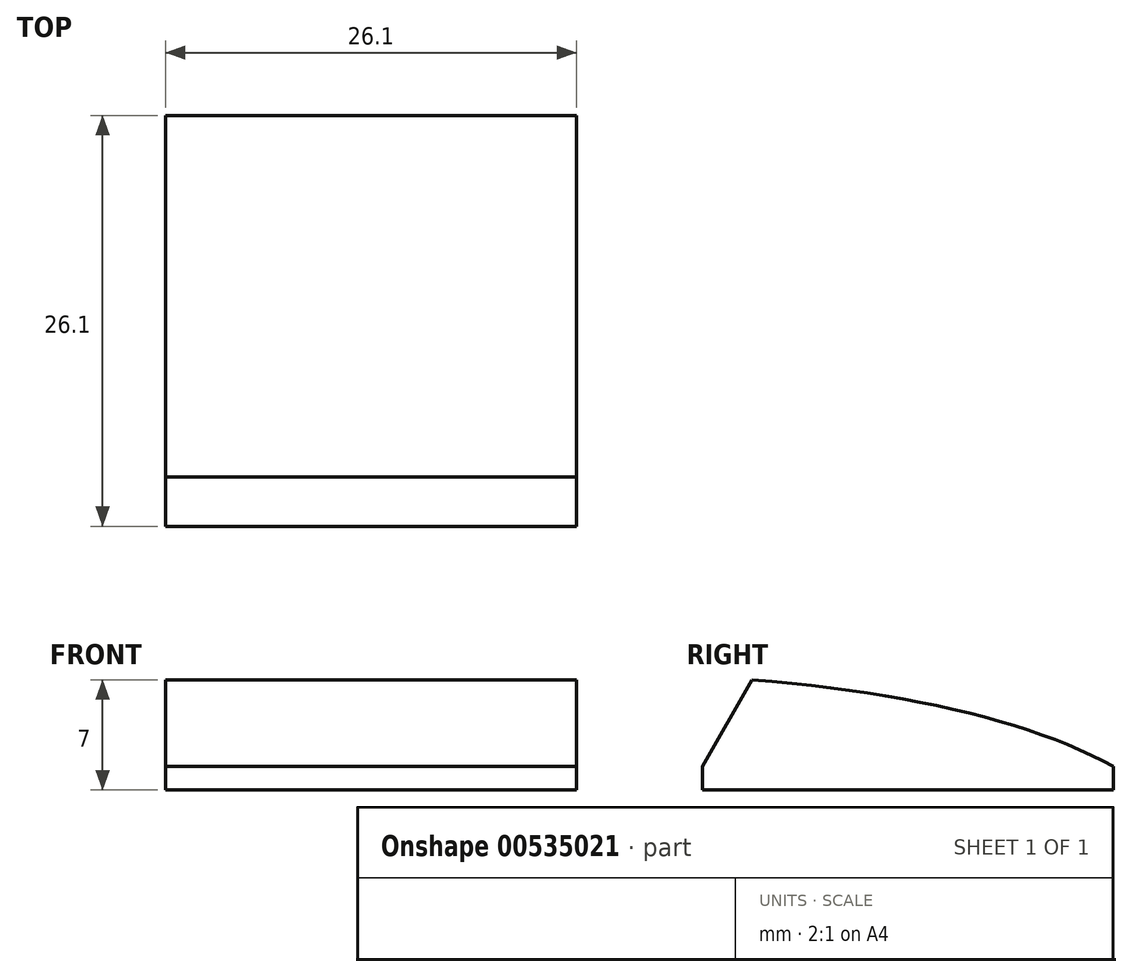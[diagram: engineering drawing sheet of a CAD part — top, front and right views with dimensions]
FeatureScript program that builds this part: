
annotation { "Feature Type Name" : "Feature", "Feature Type Description" : "" }
export const myFeature = defineFeature(function(context is Context, id is Id, definition is map)
    precondition{}
    {
        {
            var Q0;
            Q0=qCreatedBy(makeId("Top.planeOp"),FACE);
            var sketch = newSketch(context, id + "F0", { "sketchPlane" : qUnion([Q0])});
            skLineSegment(sketch, "E0.bottom", {"start": v(13.05, 13.05) * mm, "end": v(-13.05, 13.05) * mm});
            skLineSegment(sketch, "E0.top", {"start": v(13.05, -13.05) * mm, "end": v(-13.05, -13.05) * mm});
            skLineSegment(sketch, "E0.left", {"start": v(13.05, 13.05) * mm, "end": v(13.05, -13.05) * mm});
            skLineSegment(sketch, "E0.right", {"start": v(-13.05, 13.05) * mm, "end": v(-13.05, -13.05) * mm});
            skPoint(sketch, "E0.middle", {"position": v(0, 0) * mm});
            skPoint(sketch, "E1", {"position": v(-10, 10) * mm});
            skPoint(sketch, "E2.MirrorP", {"position": v(10, 10) * mm});
            skPoint(sketch, "E3.MirrorP", {"position": v(-10, -10) * mm});
            skPoint(sketch, "E4.MirrorP", {"position": v(10, -10) * mm});
            skSolve(sketch);
        }
        {
            var Q0;
            Q0=makeQuery(id+"F0.imprint","IMPRINT",FACE,{"disambiguationData":[TD([[makeQuery(id+"F0.imprint","IMPRINT",EDGE,{"derivedFrom":sQuery(id+"F0.wireOp",EDGE,"E0.bottom")}),1.0]])]});
            extrude(context, id + "F1", {"entities" : qUnion([Q0]), "depth" : 7 * mm, "offsetDistance" : 25 * mm});
        }
        {
            var Q0;
            Q0=makeQuery(id+"F1.opExtrude","SWEPT_FACE",FACE,{"disambiguationData":[OSD([sQuery(id+"F0.wireOp",EDGE,"E0.left")])]});
            var sketch = newSketch(context, id + "F2", { "sketchPlane" : qUnion([Q0])});
            skLineSegment(sketch, "E5", {"start": v(-13.05, 1.5) * mm, "end": v(-9.9, 7) * mm});
            skFitSpline(sketch, "E6", {"points": [v(-9.9, 7) * mm, v(13.05, 1.5) * mm], "startDerivative": vector(29.71, -2.32) * mm, "endDerivative": vector(15.38, -8.44) * mm});
            skSolve(sketch);
        }
        {
            var Q0;
            {var subQ0=sQuery(id+"F2.wireOp",EDGE,"E5");Q0=makeQuery(id+"F2.imprint","IMPRINT",FACE,{"disambiguationData":[TD([[makeQuery(id+"F2.imprint","IMPRINT",EDGE,{"derivedFrom":subQ0}),1.0]])]});}
            var Q1;
            {var subQ0=sQuery(id+"F2.wireOp",EDGE,"E6");Q1=makeQuery(id+"F2.imprint","IMPRINT",FACE,{"disambiguationData":[TD([[makeQuery(id+"F2.imprint","IMPRINT",EDGE,{"derivedFrom":subQ0}),1.0]])]});}
            extrude(context, id + "F3", {"entities" : qUnion([Q0, Q1]), "operationType" : NewBodyOperationType.REMOVE, "endBound" : BoundingType.THROUGH_ALL, "oppositeDirection" : true, "depth" : 25 * mm, "offsetDistance" : 25 * mm});
        }
    });
